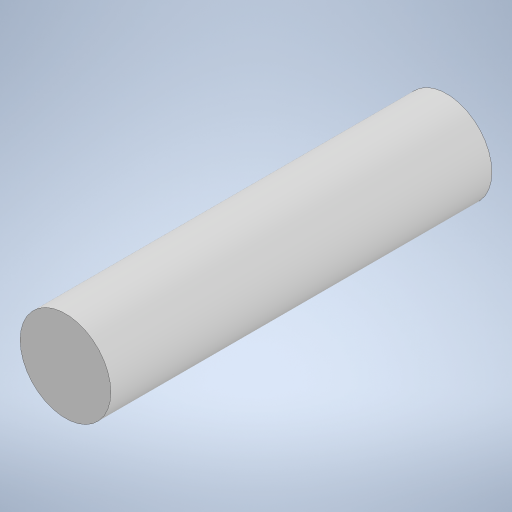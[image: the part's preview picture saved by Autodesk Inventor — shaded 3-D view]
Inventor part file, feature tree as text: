
AUTODESK INVENTOR PART (.ipt)
format: ipt  version: 2023.5 (Build 275446000, 446)  size: 218,112 bytes
history: native  units: in
note: dims shown in document units (in); Inventor stores cm internally (conversion verified against a paired STEP export)
features: extrude x2, sketch x2
ambient origin geometry x8: Origin, YZ Plane, XZ Plane, XY Plane, X Axis, Y Axis, Z Axis, Center Point
bodies: Solid1 (feature_tree)
feature tree (4):
  extrude  "Extrusion1"  Depth=0.4134in TaperAngle=0.0deg
  extrude  "Extrusion2"  Depth=0.2953in TaperAngle=0.0deg
  sketch  "Sketch1"  dims[d0=0.0984in d1=0.4134in d2=0.0in]
  sketch  "Sketch2"  dims[d3=0.0591in d4=0.2953in d5=0.0in d6=0.0197in d7=0.0344in d8=0.0197in d9=0.0344in]
